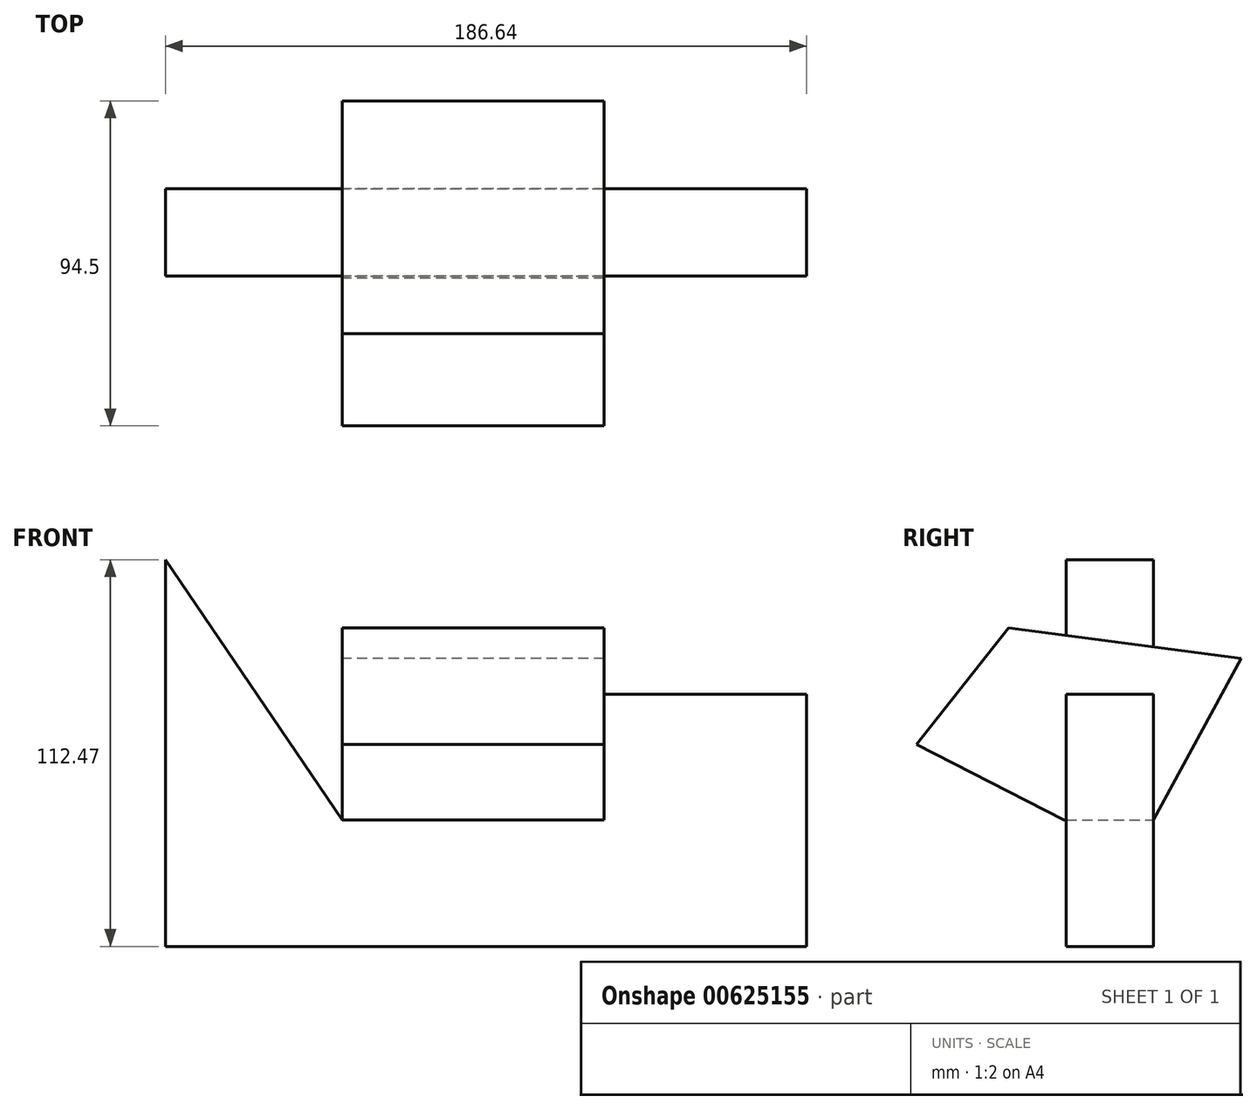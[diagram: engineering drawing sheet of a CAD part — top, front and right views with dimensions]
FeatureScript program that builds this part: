
annotation { "Feature Type Name" : "Feature", "Feature Type Description" : "" }
export const myFeature = defineFeature(function(context is Context, id is Id, definition is map)
    precondition{}
    {
        {
            var Q0;
            Q0=qCreatedBy(makeId("Front.planeOp"),FACE);
            var sketch = newSketch(context, id + "F0", { "sketchPlane" : qUnion([Q0])});
            skLineSegment(sketch, "E0.top", {"start": v(-51.55, -36.84) * mm, "end": v(58.89, -36.84) * mm});
            skLineSegment(sketch, "E0.left", {"start": v(-51.55, 75.63) * mm, "end": v(-51.55, -36.84) * mm});
            skLineSegment(sketch, "E0.right", {"start": v(58.89, 36.57) * mm, "end": v(58.89, -36.84) * mm});
            skLineSegment(sketch, "E1", {"start": v(-51.55, 75.63) * mm, "end": v(0, 0) * mm});
            skLineSegment(sketch, "E2", {"start": v(0, 0) * mm, "end": v(58.89, 36.57) * mm});
            skSolve(sketch);
        }
        {
            var Q0;
            Q0 = qSketchRegion(id + "F0", true);
            extrude(context, id + "F1", {"entities" : qUnion([Q0]), "depth" : 25.4 * mm, "offsetDistance" : 25.4 * mm});
        }
        {
            var Q0;
            Q0=qCreatedBy(makeId("Right.planeOp"),FACE);
            var sketch = newSketch(context, id + "F2", { "sketchPlane" : qUnion([Q0])});
            skLineSegment(sketch, "E3", {"start": v(-26.03, 0) * mm, "end": v(-68.98, 21.92) * mm});
            skLineSegment(sketch, "E4", {"start": v(-68.98, 21.92) * mm, "end": v(-42.24, 55.88) * mm});
            skLineSegment(sketch, "E5", {"start": v(-42.24, 55.88) * mm, "end": v(25.52, 46.9) * mm});
            skLineSegment(sketch, "E6", {"start": v(25.52, 46.9) * mm, "end": v(0, 0) * mm});
            skLineSegment(sketch, "E7", {"start": v(0, 0) * mm, "end": v(-26.03, 0) * mm});
            skSolve(sketch);
        }
        {
            var Q0;
            Q0 = qSketchRegion(id + "F2", true);
            var Q1;
            Q1=makeQuery(id+"F1.opExtrude","SWEPT_FACE",FACE,{"disambiguationData":[OSD([sQuery(id+"F0.wireOp",EDGE,"E0.right")])]});
            extrude(context, id + "F3", {"entities" : qUnion([Q0, Q1]), "operationType" : NewBodyOperationType.ADD, "depth" : 76.2 * mm, "offsetDistance" : 25.4 * mm});
        }
    });
